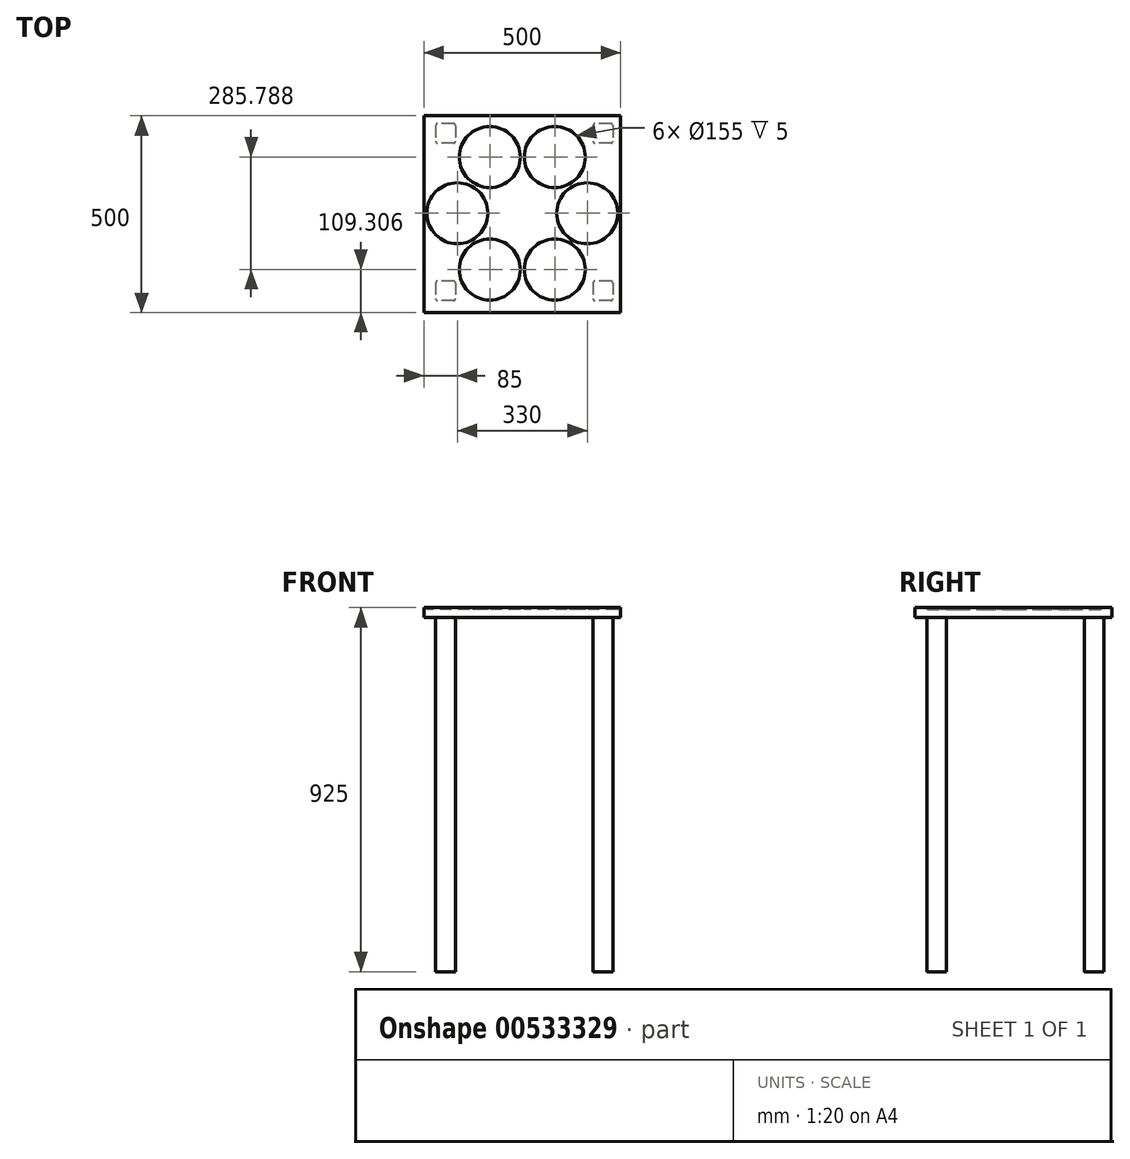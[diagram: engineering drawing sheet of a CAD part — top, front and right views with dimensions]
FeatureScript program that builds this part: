
annotation { "Feature Type Name" : "Feature", "Feature Type Description" : "" }
export const myFeature = defineFeature(function(context is Context, id is Id, definition is map)
    precondition{}
    {
        {
            var Q0;
            Q0=qCreatedBy(makeId("Top.planeOp"),FACE);
            var sketch = newSketch(context, id + "F0", { "sketchPlane" : qUnion([Q0])});
            skCircle(sketch, "E0", {"center": v(-165, 0) * mm, "radius": 77.5 * mm});
            skLineSegment(sketch, "E1.bottom", {"start": v(-250, 247.8) * mm, "end": v(250, 247.8) * mm});
            skLineSegment(sketch, "E1.top", {"start": v(-250, -252.2) * mm, "end": v(250, -252.2) * mm});
            skLineSegment(sketch, "E1.left", {"start": v(-250, 247.8) * mm, "end": v(-250, -252.2) * mm});
            skLineSegment(sketch, "E1.right", {"start": v(250, 247.8) * mm, "end": v(250, -252.2) * mm});
            skCircle(sketch, "E2.1.0", {"center": v(-82.5, -142.9) * mm, "radius": 77.5 * mm});
            skCircle(sketch, "E2.2.0", {"center": v(82.5, -142.9) * mm, "radius": 77.5 * mm});
            skCircle(sketch, "E2.3.0", {"center": v(165, 0) * mm, "radius": 77.5 * mm});
            skCircle(sketch, "E2.4.0", {"center": v(82.5, 142.9) * mm, "radius": 77.5 * mm});
            skCircle(sketch, "E2.5.0", {"center": v(-82.5, 142.9) * mm, "radius": 77.5 * mm});
            skPoint(sketch, "E2.center", {"position": v(0, 0) * mm});
            skSolve(sketch);
        }
        {
            var Q0;
            Q0=makeQuery(id+"F0.imprint","IMPRINT",FACE,{"disambiguationData":[TD([[makeQuery(id+"F0.imprint","IMPRINT",EDGE,{"derivedFrom":sQuery(id+"F0.wireOp",EDGE,"E0")}),-1.0]])]});
            var Q1;
            Q1=makeQuery(id+"F0.imprint","IMPRINT",FACE,{"disambiguationData":[TD([[makeQuery(id+"F0.imprint","IMPRINT",EDGE,{"derivedFrom":sQuery(id+"F0.wireOp",EDGE,"E2.5.0")}),1.0]])]});
            var Q2;
            Q2=makeQuery(id+"F0.imprint","IMPRINT",FACE,{"disambiguationData":[TD([[makeQuery(id+"F0.imprint","IMPRINT",EDGE,{"derivedFrom":sQuery(id+"F0.wireOp",EDGE,"E2.4.0")}),1.0]])]});
            var Q3;
            Q3=makeQuery(id+"F0.imprint","IMPRINT",FACE,{"disambiguationData":[TD([[makeQuery(id+"F0.imprint","IMPRINT",EDGE,{"derivedFrom":sQuery(id+"F0.wireOp",EDGE,"E2.3.0")}),1.0]])]});
            var Q4;
            Q4=makeQuery(id+"F0.imprint","IMPRINT",FACE,{"disambiguationData":[TD([[makeQuery(id+"F0.imprint","IMPRINT",EDGE,{"derivedFrom":sQuery(id+"F0.wireOp",EDGE,"E0")}),1.0]])]});
            var Q5;
            Q5=makeQuery(id+"F0.imprint","IMPRINT",FACE,{"disambiguationData":[TD([[makeQuery(id+"F0.imprint","IMPRINT",EDGE,{"derivedFrom":sQuery(id+"F0.wireOp",EDGE,"E2.1.0")}),1.0]])]});
            var Q6;
            Q6=makeQuery(id+"F0.imprint","IMPRINT",FACE,{"disambiguationData":[TD([[makeQuery(id+"F0.imprint","IMPRINT",EDGE,{"derivedFrom":sQuery(id+"F0.wireOp",EDGE,"E2.2.0")}),1.0]])]});
            extrude(context, id + "F1", {"entities" : qUnion([Q0, Q1, Q2, Q3, Q4, Q5, Q6]), "oppositeDirection" : true, "depth" : 25 * mm, "offsetDistance" : 25 * mm});
        }
        {
            var Q0;
            Q0=makeQuery(id+"F0.imprint","IMPRINT",FACE,{"disambiguationData":[TD([[makeQuery(id+"F0.imprint","IMPRINT",EDGE,{"derivedFrom":sQuery(id+"F0.wireOp",EDGE,"E2.5.0")}),1.0]])]});
            var Q1;
            Q1=makeQuery(id+"F0.imprint","IMPRINT",FACE,{"disambiguationData":[TD([[makeQuery(id+"F0.imprint","IMPRINT",EDGE,{"derivedFrom":sQuery(id+"F0.wireOp",EDGE,"E2.4.0")}),1.0]])]});
            var Q2;
            Q2=makeQuery(id+"F0.imprint","IMPRINT",FACE,{"disambiguationData":[TD([[makeQuery(id+"F0.imprint","IMPRINT",EDGE,{"derivedFrom":sQuery(id+"F0.wireOp",EDGE,"E2.3.0")}),1.0]])]});
            var Q3;
            Q3=makeQuery(id+"F0.imprint","IMPRINT",FACE,{"disambiguationData":[TD([[makeQuery(id+"F0.imprint","IMPRINT",EDGE,{"derivedFrom":sQuery(id+"F0.wireOp",EDGE,"E2.2.0")}),1.0]])]});
            var Q4;
            Q4=makeQuery(id+"F0.imprint","IMPRINT",FACE,{"disambiguationData":[TD([[makeQuery(id+"F0.imprint","IMPRINT",EDGE,{"derivedFrom":sQuery(id+"F0.wireOp",EDGE,"E2.1.0")}),1.0]])]});
            var Q5;
            Q5=makeQuery(id+"F0.imprint","IMPRINT",FACE,{"disambiguationData":[TD([[makeQuery(id+"F0.imprint","IMPRINT",EDGE,{"derivedFrom":sQuery(id+"F0.wireOp",EDGE,"E0")}),1.0]])]});
            extrude(context, id + "F2", {"entities" : qUnion([Q0, Q1, Q2, Q3, Q4, Q5]), "operationType" : NewBodyOperationType.REMOVE, "oppositeDirection" : true, "depth" : 5 * mm, "offsetDistance" : 25 * mm});
        }
        {
            var Q0;
            Q0=makeQuery(id+"F1.opExtrude","CAP_FACE",FACE,{"disambiguationData":[OSD([sQuery(id+"F0.wireOp",EDGE,"E1.bottom"),sQuery(id+"F0.wireOp",EDGE,"E1.top"),sQuery(id+"F0.wireOp",EDGE,"E1.left"),sQuery(id+"F0.wireOp",EDGE,"E1.right")])],"isStart":false});
            var sketch = newSketch(context, id + "F3", { "sketchPlane" : qUnion([Q0])});
            skLineSegment(sketch, "E3.bottom", {"start": v(225, -227.8) * mm, "end": v(185, -227.8) * mm});
            skLineSegment(sketch, "E3.top", {"start": v(225, -177.8) * mm, "end": v(185, -177.8) * mm});
            skLineSegment(sketch, "E3.left", {"start": v(230, -222.8) * mm, "end": v(230, -182.8) * mm});
            skLineSegment(sketch, "E3.right", {"start": v(180, -222.8) * mm, "end": v(180, -182.8) * mm});
            skPoint(sketch, "E4.visualSharp", {"position": v(230, -177.8) * mm});
            skArc(sketch, "E4.filletArc", {"start": v(230, -182.8) * mm, "mid": v(228.54, -179.27) * mm, "end": v(225, -177.8) * mm});
            skPoint(sketch, "E5.visualSharp", {"position": v(230, -227.8) * mm});
            skArc(sketch, "E5.filletArc", {"start": v(225, -227.8) * mm, "mid": v(228.54, -226.34) * mm, "end": v(230, -222.8) * mm});
            skPoint(sketch, "E6.visualSharp", {"position": v(180, -227.8) * mm});
            skArc(sketch, "E6.filletArc", {"start": v(180, -222.8) * mm, "mid": v(181.46, -226.34) * mm, "end": v(185, -227.8) * mm});
            skPoint(sketch, "E7.visualSharp", {"position": v(180, -177.8) * mm});
            skArc(sketch, "E7.filletArc", {"start": v(185, -177.8) * mm, "mid": v(181.46, -179.27) * mm, "end": v(180, -182.8) * mm});
            skPoint(sketch, "E8.0.1.0", {"position": v(230, 222.2) * mm});
            skPoint(sketch, "E8.0.1.1", {"position": v(180, 222.2) * mm});
            skLineSegment(sketch, "E8.0.1.2", {"start": v(230, 177.2) * mm, "end": v(230, 217.2) * mm});
            skLineSegment(sketch, "E8.0.1.3", {"start": v(225, 222.2) * mm, "end": v(185, 222.2) * mm});
            skLineSegment(sketch, "E8.0.1.4", {"start": v(180, 177.2) * mm, "end": v(180, 217.2) * mm});
            skPoint(sketch, "E8.0.1.5", {"position": v(180, 172.2) * mm});
            skLineSegment(sketch, "E8.0.1.6", {"start": v(225, 172.2) * mm, "end": v(185, 172.2) * mm});
            skPoint(sketch, "E8.0.1.7", {"position": v(230, 172.2) * mm});
            skArc(sketch, "E8.0.1.8", {"start": v(185, 222.2) * mm, "mid": v(181.46, 220.73) * mm, "end": v(180, 217.2) * mm});
            skArc(sketch, "E8.0.1.9", {"start": v(230, 217.2) * mm, "mid": v(228.54, 220.73) * mm, "end": v(225, 222.2) * mm});
            skArc(sketch, "E8.0.1.10", {"start": v(225, 172.2) * mm, "mid": v(228.54, 173.66) * mm, "end": v(230, 177.2) * mm});
            skArc(sketch, "E8.0.1.11", {"start": v(180, 177.2) * mm, "mid": v(181.46, 173.66) * mm, "end": v(185, 172.2) * mm});
            skPoint(sketch, "E8.1.0.0", {"position": v(-170, -177.8) * mm});
            skPoint(sketch, "E8.1.0.1", {"position": v(-220, -177.8) * mm});
            skLineSegment(sketch, "E8.1.0.2", {"start": v(-170, -222.8) * mm, "end": v(-170, -182.8) * mm});
            skLineSegment(sketch, "E8.1.0.3", {"start": v(-175, -177.8) * mm, "end": v(-215, -177.8) * mm});
            skLineSegment(sketch, "E8.1.0.4", {"start": v(-220, -222.8) * mm, "end": v(-220, -182.8) * mm});
            skPoint(sketch, "E8.1.0.5", {"position": v(-220, -227.8) * mm});
            skLineSegment(sketch, "E8.1.0.6", {"start": v(-175, -227.8) * mm, "end": v(-215, -227.8) * mm});
            skPoint(sketch, "E8.1.0.7", {"position": v(-170, -227.8) * mm});
            skArc(sketch, "E8.1.0.8", {"start": v(-215, -177.8) * mm, "mid": v(-218.54, -179.27) * mm, "end": v(-220, -182.8) * mm});
            skArc(sketch, "E8.1.0.9", {"start": v(-170, -182.8) * mm, "mid": v(-171.46, -179.27) * mm, "end": v(-175, -177.8) * mm});
            skArc(sketch, "E8.1.0.10", {"start": v(-175, -227.8) * mm, "mid": v(-171.46, -226.34) * mm, "end": v(-170, -222.8) * mm});
            skArc(sketch, "E8.1.0.11", {"start": v(-220, -222.8) * mm, "mid": v(-218.54, -226.34) * mm, "end": v(-215, -227.8) * mm});
            skPoint(sketch, "E8.1.1.0", {"position": v(-170, 222.2) * mm});
            skPoint(sketch, "E8.1.1.1", {"position": v(-220, 222.2) * mm});
            skLineSegment(sketch, "E8.1.1.2", {"start": v(-170, 177.2) * mm, "end": v(-170, 217.2) * mm});
            skLineSegment(sketch, "E8.1.1.3", {"start": v(-175, 222.2) * mm, "end": v(-215, 222.2) * mm});
            skLineSegment(sketch, "E8.1.1.4", {"start": v(-220, 177.2) * mm, "end": v(-220, 217.2) * mm});
            skPoint(sketch, "E8.1.1.5", {"position": v(-220, 172.2) * mm});
            skLineSegment(sketch, "E8.1.1.6", {"start": v(-175, 172.2) * mm, "end": v(-215, 172.2) * mm});
            skPoint(sketch, "E8.1.1.7", {"position": v(-170, 172.2) * mm});
            skArc(sketch, "E8.1.1.8", {"start": v(-215, 222.2) * mm, "mid": v(-218.54, 220.73) * mm, "end": v(-220, 217.2) * mm});
            skArc(sketch, "E8.1.1.9", {"start": v(-170, 217.2) * mm, "mid": v(-171.46, 220.73) * mm, "end": v(-175, 222.2) * mm});
            skArc(sketch, "E8.1.1.10", {"start": v(-175, 172.2) * mm, "mid": v(-171.46, 173.66) * mm, "end": v(-170, 177.2) * mm});
            skArc(sketch, "E8.1.1.11", {"start": v(-220, 177.2) * mm, "mid": v(-218.54, 173.66) * mm, "end": v(-215, 172.2) * mm});
            skLineSegment(sketch, "E8.direction1", {"start": v(180, -227.8) * mm, "end": v(-220, -227.8) * mm, "construction": true});
            skLineSegment(sketch, "E8.direction2", {"start": v(180, -227.8) * mm, "end": v(180, 172.2) * mm, "construction": true});
            skSolve(sketch);
        }
        {
            var Q0;
            Q0=makeQuery(id+"F3.imprint","IMPRINT",FACE,{"disambiguationData":[TD([[makeQuery(id+"F3.imprint","IMPRINT",EDGE,{"derivedFrom":sQuery(id+"F3.wireOp",EDGE,"E8.0.1.2")}),1.0]])]});
            var Q1;
            Q1=makeQuery(id+"F3.imprint","IMPRINT",FACE,{"disambiguationData":[TD([[makeQuery(id+"F3.imprint","IMPRINT",EDGE,{"derivedFrom":sQuery(id+"F3.wireOp",EDGE,"E8.1.1.2")}),1.0]])]});
            var Q2;
            Q2=makeQuery(id+"F3.imprint","IMPRINT",FACE,{"disambiguationData":[TD([[makeQuery(id+"F3.imprint","IMPRINT",EDGE,{"derivedFrom":sQuery(id+"F3.wireOp",EDGE,"E8.1.0.2")}),1.0]])]});
            var Q3;
            Q3=makeQuery(id+"F3.imprint","IMPRINT",FACE,{"disambiguationData":[TD([[makeQuery(id+"F3.imprint","IMPRINT",EDGE,{"derivedFrom":sQuery(id+"F3.wireOp",EDGE,"E3.bottom")}),-1.0]])]});
            extrude(context, id + "F4", {"entities" : qUnion([Q0, Q1, Q2, Q3]), "operationType" : NewBodyOperationType.ADD, "depth" : 900 * mm, "offsetDistance" : 25 * mm});
        }
    });
